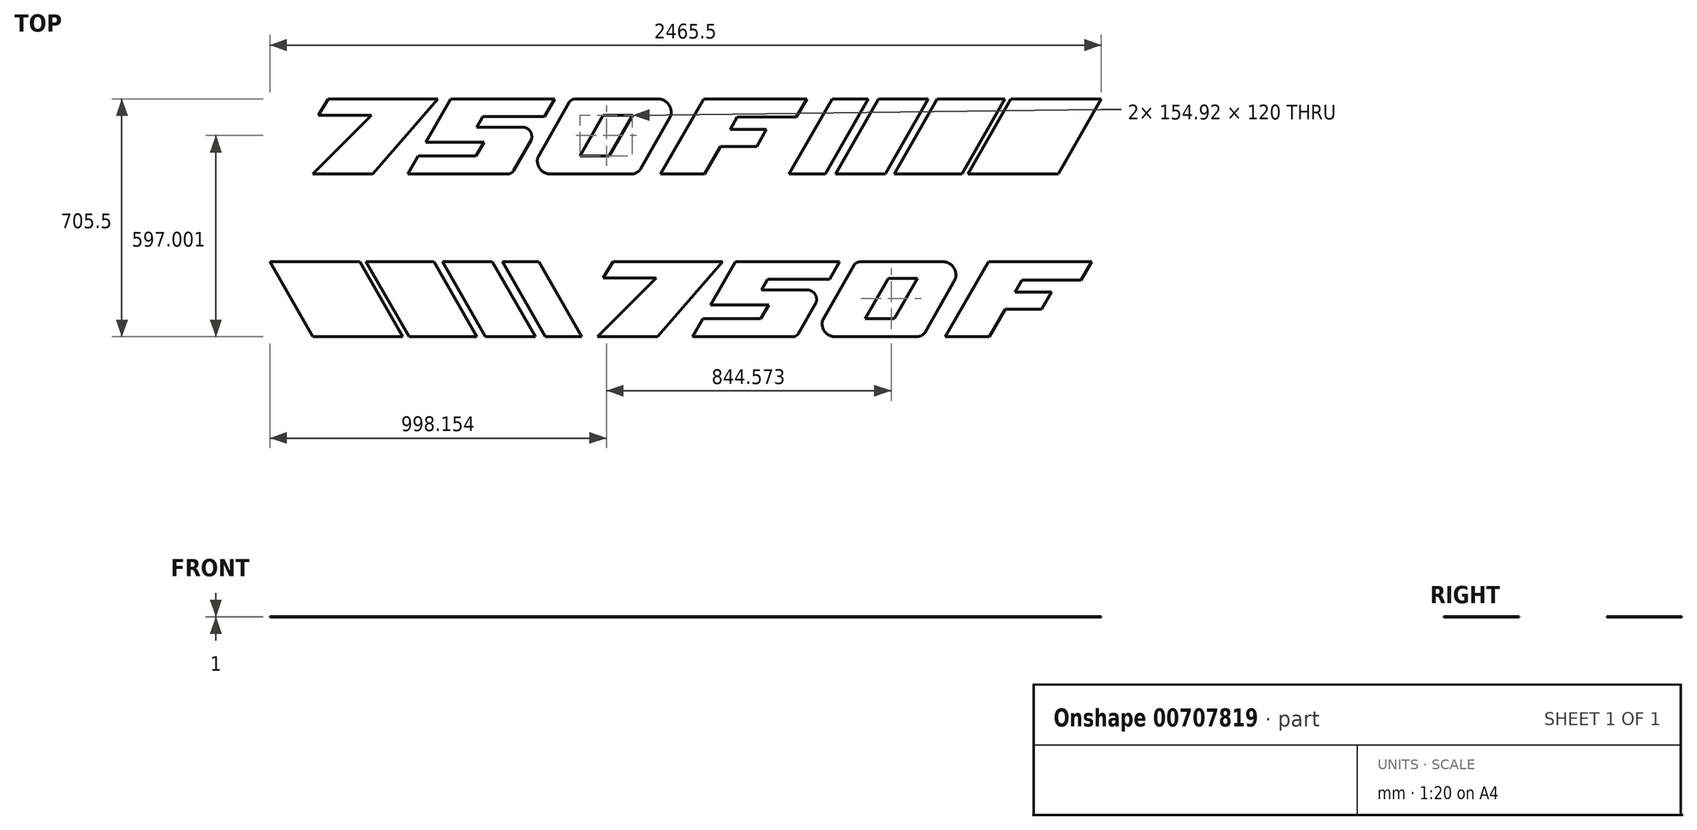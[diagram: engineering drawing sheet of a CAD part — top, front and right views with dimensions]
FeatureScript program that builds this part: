
annotation { "Feature Type Name" : "Feature", "Feature Type Description" : "" }
export const myFeature = defineFeature(function(context is Context, id is Id, definition is map)
    precondition{}
    {
        {
            var Q0;
            Q0=qCreatedBy(makeId("Top.planeOp"),FACE);
            var sketch = newSketch(context, id + "F0", { "sketchPlane" : qUnion([Q0])});
            skLineSegment(sketch, "E0", {"start": v(-1075.65, 281.14) * mm, "end": v(-750.23, 281.14) * mm});
            skLineSegment(sketch, "E1", {"start": v(-839.48, 58.67) * mm, "end": v(-542.36, 58.67) * mm});
            skLineSegment(sketch, "E2", {"start": v(-1105.04, 233.16) * mm, "end": v(-1075.65, 281.14) * mm});
            skLineSegment(sketch, "E3", {"start": v(-1105.04, 233.16) * mm, "end": v(-946.87, 233.16) * mm});
            skLineSegment(sketch, "E4", {"start": v(-946.87, 233.16) * mm, "end": v(-1121.46, 58.67) * mm});
            skLineSegment(sketch, "E5", {"start": v(-1121.46, 58.67) * mm, "end": v(-943.52, 58.67) * mm});
            skLineSegment(sketch, "E6", {"start": v(418.91, 281.14) * mm, "end": v(291.85, 58.67) * mm});
            skLineSegment(sketch, "E7", {"start": v(526.29, 281.14) * mm, "end": v(399.23, 58.67) * mm});
            skLineSegment(sketch, "E8", {"start": v(556.71, 281.14) * mm, "end": v(429.65, 58.67) * mm});
            skLineSegment(sketch, "E9", {"start": v(704.09, 281.14) * mm, "end": v(577.03, 58.67) * mm});
            skLineSegment(sketch, "E10", {"start": v(730.63, 281.14) * mm, "end": v(603.57, 58.67) * mm});
            skLineSegment(sketch, "E11", {"start": v(931.31, 281.14) * mm, "end": v(804.25, 58.67) * mm});
            skLineSegment(sketch, "E12", {"start": v(949.16, 281.14) * mm, "end": v(822.1, 58.67) * mm});
            skLineSegment(sketch, "E13", {"start": v(1216.97, 281.14) * mm, "end": v(1089.9, 58.67) * mm});
            skLineSegment(sketch, "E14", {"start": v(37.9, 281.14) * mm, "end": v(-89.16, 58.67) * mm});
            skLineSegment(sketch, "E15", {"start": v(137.83, 227.23) * mm, "end": v(117, 190.76) * mm});
            skLineSegment(sketch, "E16", {"start": v(344.12, 281.14) * mm, "end": v(313.33, 227.23) * mm});
            skLineSegment(sketch, "E17", {"start": v(137.83, 227.23) * mm, "end": v(313.33, 227.23) * mm});
            skLineSegment(sketch, "E18", {"start": v(117, 190.76) * mm, "end": v(224.56, 190.76) * mm});
            skLineSegment(sketch, "E19", {"start": v(88.26, 140.43) * mm, "end": v(195.82, 140.43) * mm});
            skLineSegment(sketch, "E20.trimOffspring", {"start": v(224.56, 190.76) * mm, "end": v(195.82, 140.43) * mm});
            skLineSegment(sketch, "E21.trimOffspring", {"start": v(88.26, 140.43) * mm, "end": v(41.56, 58.67) * mm});
            skLineSegment(sketch, "E22", {"start": v(-943.52, 58.67) * mm, "end": v(-750.23, 281.14) * mm});
            skLineSegment(sketch, "E23", {"start": v(-712.42, 281.14) * mm, "end": v(-785.6, 153.03) * mm});
            skLineSegment(sketch, "E24", {"start": v(-403.6, 281.14) * mm, "end": v(-433.3, 229.15) * mm});
            skLineSegment(sketch, "E25", {"start": v(-360.22, 271.8) * mm, "end": v(-453.2, 109) * mm});
            skLineSegment(sketch, "E26", {"start": v(-259.3, 232.64) * mm, "end": v(-327.84, 112.64) * mm});
            skLineSegment(sketch, "E27", {"start": v(-172.92, 232.64) * mm, "end": v(-241.45, 112.64) * mm});
            skLineSegment(sketch, "E28", {"start": v(-60.53, 229.18) * mm, "end": v(-150, 72.51) * mm});
            skLineSegment(sketch, "E29", {"start": v(-785.6, 153.03) * mm, "end": v(-613.24, 153.03) * mm});
            skLineSegment(sketch, "E30", {"start": v(-613.24, 153.03) * mm, "end": v(-636.6, 112.13) * mm});
            skLineSegment(sketch, "E31", {"start": v(-636.6, 112.13) * mm, "end": v(-808.95, 112.13) * mm});
            skLineSegment(sketch, "E32", {"start": v(-433.3, 229.15) * mm, "end": v(-616.43, 229.15) * mm});
            skLineSegment(sketch, "E33", {"start": v(-616.43, 229.15) * mm, "end": v(-634.47, 197.56) * mm});
            skLineSegment(sketch, "E34", {"start": v(-634.47, 197.56) * mm, "end": v(-496.87, 197.56) * mm});
            skLineSegment(sketch, "E35", {"start": v(-259.3, 232.64) * mm, "end": v(-172.92, 232.64) * mm});
            skLineSegment(sketch, "E36", {"start": v(-327.84, 112.64) * mm, "end": v(-241.45, 112.64) * mm});
            skLineSegment(sketch, "E37.trimOffspring", {"start": v(-808.95, 112.13) * mm, "end": v(-839.48, 58.67) * mm});
            skLineSegment(sketch, "E38.trimOffspring", {"start": v(-472.9, 159.8) * mm, "end": v(-524.88, 68.8) * mm});
            skLineSegment(sketch, "E39.trimOffspring", {"start": v(-712.42, 281.14) * mm, "end": v(-403.6, 281.14) * mm});
            skLineSegment(sketch, "E40.trimOffspring", {"start": v(-344.14, 281.14) * mm, "end": v(-92.2, 281.14) * mm});
            skLineSegment(sketch, "E41.trimOffspring", {"start": v(-416.83, 58.67) * mm, "end": v(-174.5, 58.67) * mm});
            skLineSegment(sketch, "E42.trimOffspring", {"start": v(-89.16, 58.67) * mm, "end": v(41.56, 58.67) * mm});
            skLineSegment(sketch, "E43.trimOffspring", {"start": v(37.9, 281.14) * mm, "end": v(344.12, 281.14) * mm});
            skLineSegment(sketch, "E44.trimOffspring", {"start": v(418.91, 281.14) * mm, "end": v(526.29, 281.14) * mm});
            skLineSegment(sketch, "E45.trimOffspring", {"start": v(291.85, 58.67) * mm, "end": v(399.23, 58.67) * mm});
            skLineSegment(sketch, "E46.trimOffspring", {"start": v(429.65, 58.67) * mm, "end": v(577.03, 58.67) * mm});
            skLineSegment(sketch, "E47.trimOffspring", {"start": v(556.71, 281.14) * mm, "end": v(704.09, 281.14) * mm});
            skLineSegment(sketch, "E48.trimOffspring", {"start": v(603.57, 58.67) * mm, "end": v(804.25, 58.67) * mm});
            skLineSegment(sketch, "E49.trimOffspring", {"start": v(730.63, 281.14) * mm, "end": v(931.31, 281.14) * mm});
            skLineSegment(sketch, "E50.trimOffspring", {"start": v(949.16, 281.14) * mm, "end": v(1216.97, 281.14) * mm});
            skLineSegment(sketch, "E51.trimOffspring", {"start": v(822.1, 58.67) * mm, "end": v(1089.9, 58.67) * mm});
            skArc(sketch, "E52", {"start": v(-472.9, 159.8) * mm, "mid": v(-475.61, 184.57) * mm, "end": v(-496.87, 197.56) * mm});
            skArc(sketch, "E53", {"start": v(-542.36, 58.67) * mm, "mid": v(-532.33, 61.52) * mm, "end": v(-524.88, 68.8) * mm});
            skArc(sketch, "E54", {"start": v(-453.2, 109) * mm, "mid": v(-447.59, 74.75) * mm, "end": v(-416.83, 58.67) * mm});
            skArc(sketch, "E55", {"start": v(-60.53, 229.18) * mm, "mid": v(-63.93, 262.74) * mm, "end": v(-92.2, 281.14) * mm});
            skArc(sketch, "E56", {"start": v(-174.5, 58.67) * mm, "mid": v(-160.63, 62.73) * mm, "end": v(-150, 72.51) * mm});
            skArc(sketch, "E57", {"start": v(-344.14, 281.14) * mm, "mid": v(-353.26, 278.33) * mm, "end": v(-360.22, 271.8) * mm});
            skLineSegment(sketch, "E58", {"start": v(-231.08, -201.9) * mm, "end": v(94.34, -201.9) * mm});
            skLineSegment(sketch, "E59", {"start": v(5.09, -424.36) * mm, "end": v(302.22, -424.36) * mm});
            skLineSegment(sketch, "E60", {"start": v(-260.47, -249.87) * mm, "end": v(-231.08, -201.9) * mm});
            skLineSegment(sketch, "E61", {"start": v(-260.47, -249.87) * mm, "end": v(-102.3, -249.87) * mm});
            skLineSegment(sketch, "E62", {"start": v(-102.3, -249.87) * mm, "end": v(-276.9, -424.36) * mm});
            skLineSegment(sketch, "E63", {"start": v(-276.9, -424.36) * mm, "end": v(-98.95, -424.36) * mm});
            skLineSegment(sketch, "E64", {"start": v(882.48, -201.9) * mm, "end": v(755.41, -424.36) * mm});
            skLineSegment(sketch, "E65", {"start": v(982.4, -255.8) * mm, "end": v(961.58, -292.27) * mm});
            skLineSegment(sketch, "E66", {"start": v(1188.7, -201.9) * mm, "end": v(1157.9, -255.8) * mm});
            skLineSegment(sketch, "E67", {"start": v(982.4, -255.8) * mm, "end": v(1157.9, -255.8) * mm});
            skLineSegment(sketch, "E68", {"start": v(961.58, -292.27) * mm, "end": v(1069.14, -292.27) * mm});
            skLineSegment(sketch, "E69", {"start": v(932.83, -342.6) * mm, "end": v(1040.4, -342.6) * mm});
            skLineSegment(sketch, "E70.trimOffspring", {"start": v(1069.14, -292.27) * mm, "end": v(1040.4, -342.6) * mm});
            skLineSegment(sketch, "E71.trimOffspring", {"start": v(932.83, -342.6) * mm, "end": v(886.14, -424.36) * mm});
            skLineSegment(sketch, "E72", {"start": v(-98.95, -424.36) * mm, "end": v(94.34, -201.9) * mm});
            skLineSegment(sketch, "E73", {"start": v(132.15, -201.9) * mm, "end": v(58.98, -330) * mm});
            skLineSegment(sketch, "E74", {"start": v(440.97, -201.9) * mm, "end": v(411.28, -253.88) * mm});
            skLineSegment(sketch, "E75", {"start": v(484.35, -211.23) * mm, "end": v(391.37, -374.03) * mm});
            skLineSegment(sketch, "E76", {"start": v(585.27, -250.4) * mm, "end": v(516.74, -370.4) * mm});
            skLineSegment(sketch, "E77", {"start": v(671.66, -250.4) * mm, "end": v(603.12, -370.4) * mm});
            skLineSegment(sketch, "E78", {"start": v(784.05, -253.85) * mm, "end": v(694.56, -410.52) * mm});
            skLineSegment(sketch, "E79", {"start": v(58.98, -330) * mm, "end": v(231.34, -330) * mm});
            skLineSegment(sketch, "E80", {"start": v(231.34, -330) * mm, "end": v(207.97, -370.9) * mm});
            skLineSegment(sketch, "E81", {"start": v(207.97, -370.9) * mm, "end": v(35.62, -370.9) * mm});
            skLineSegment(sketch, "E82", {"start": v(411.28, -253.88) * mm, "end": v(228.14, -253.88) * mm});
            skLineSegment(sketch, "E83", {"start": v(228.14, -253.88) * mm, "end": v(210.1, -285.47) * mm});
            skLineSegment(sketch, "E84", {"start": v(210.1, -285.47) * mm, "end": v(347.7, -285.47) * mm});
            skLineSegment(sketch, "E85", {"start": v(585.27, -250.4) * mm, "end": v(671.66, -250.4) * mm});
            skLineSegment(sketch, "E86", {"start": v(516.74, -370.4) * mm, "end": v(603.12, -370.4) * mm});
            skLineSegment(sketch, "E87.trimOffspring", {"start": v(35.62, -370.9) * mm, "end": v(5.09, -424.36) * mm});
            skLineSegment(sketch, "E88.trimOffspring", {"start": v(371.67, -323.24) * mm, "end": v(319.7, -414.23) * mm});
            skLineSegment(sketch, "E89.trimOffspring", {"start": v(132.15, -201.9) * mm, "end": v(440.97, -201.9) * mm});
            skLineSegment(sketch, "E90.trimOffspring", {"start": v(500.43, -201.9) * mm, "end": v(752.38, -201.9) * mm});
            skLineSegment(sketch, "E91.trimOffspring", {"start": v(427.74, -424.36) * mm, "end": v(670.07, -424.36) * mm});
            skLineSegment(sketch, "E92.trimOffspring", {"start": v(755.41, -424.36) * mm, "end": v(886.14, -424.36) * mm});
            skLineSegment(sketch, "E93.trimOffspring", {"start": v(882.48, -201.9) * mm, "end": v(1188.7, -201.9) * mm});
            skArc(sketch, "E94", {"start": v(371.67, -323.24) * mm, "mid": v(368.96, -298.47) * mm, "end": v(347.7, -285.47) * mm});
            skArc(sketch, "E95", {"start": v(302.22, -424.36) * mm, "mid": v(312.24, -421.5) * mm, "end": v(319.7, -414.23) * mm});
            skArc(sketch, "E96", {"start": v(391.37, -374.03) * mm, "mid": v(396.99, -408.28) * mm, "end": v(427.74, -424.36) * mm});
            skArc(sketch, "E97", {"start": v(784.05, -253.85) * mm, "mid": v(780.65, -220.3) * mm, "end": v(752.38, -201.9) * mm});
            skArc(sketch, "E98", {"start": v(670.07, -424.36) * mm, "mid": v(683.94, -420.3) * mm, "end": v(694.56, -410.52) * mm});
            skArc(sketch, "E99", {"start": v(500.43, -201.9) * mm, "mid": v(491.32, -204.7) * mm, "end": v(484.35, -211.23) * mm});
            skLineSegment(sketch, "E100.MirrorCS", {"start": v(-323.4, -424.36) * mm, "end": v(-430.78, -424.36) * mm});
            skLineSegment(sketch, "E101.MirrorCS", {"start": v(-588.27, -201.9) * mm, "end": v(-461.2, -424.36) * mm});
            skLineSegment(sketch, "E102.MirrorCS", {"start": v(-635.13, -424.36) * mm, "end": v(-835.81, -424.36) * mm});
            skLineSegment(sketch, "E103.MirrorCS", {"start": v(-853.66, -424.36) * mm, "end": v(-1121.46, -424.36) * mm});
            skLineSegment(sketch, "E104.MirrorCS", {"start": v(-762.2, -201.9) * mm, "end": v(-635.13, -424.36) * mm});
            skLineSegment(sketch, "E105.MirrorCS", {"start": v(-735.65, -201.9) * mm, "end": v(-608.58, -424.36) * mm});
            skLineSegment(sketch, "E106.MirrorCS", {"start": v(-762.2, -201.9) * mm, "end": v(-962.87, -201.9) * mm});
            skLineSegment(sketch, "E107.MirrorCS", {"start": v(-962.87, -201.9) * mm, "end": v(-835.81, -424.36) * mm});
            skLineSegment(sketch, "E108.MirrorCS", {"start": v(-980.72, -201.9) * mm, "end": v(-1248.53, -201.9) * mm});
            skLineSegment(sketch, "E109.MirrorCS", {"start": v(-450.47, -201.9) * mm, "end": v(-323.4, -424.36) * mm});
            skLineSegment(sketch, "E110.MirrorCS", {"start": v(-557.85, -201.9) * mm, "end": v(-430.78, -424.36) * mm});
            skLineSegment(sketch, "E111.MirrorCS", {"start": v(-980.72, -201.9) * mm, "end": v(-853.66, -424.36) * mm});
            skLineSegment(sketch, "E112.MirrorCS", {"start": v(-461.2, -424.36) * mm, "end": v(-608.58, -424.36) * mm});
            skLineSegment(sketch, "E113.MirrorCS", {"start": v(-1248.53, -201.9) * mm, "end": v(-1121.46, -424.36) * mm});
            skLineSegment(sketch, "E114.MirrorCS", {"start": v(-450.47, -201.9) * mm, "end": v(-557.85, -201.9) * mm});
            skLineSegment(sketch, "E115.MirrorCS", {"start": v(-588.27, -201.9) * mm, "end": v(-735.65, -201.9) * mm});
            skSolve(sketch);
        }
        {
            var Q0;
            Q0=makeQuery(id+"F0.imprint","IMPRINT",FACE,{"disambiguationData":[TD([[makeQuery(id+"F0.imprint","IMPRINT",EDGE,{"derivedFrom":sQuery(id+"F0.wireOp",EDGE,"E75")}),1.0]])]});
            var Q1;
            Q1=makeQuery(id+"F0.imprint","IMPRINT",FACE,{"disambiguationData":[TD([[makeQuery(id+"F0.imprint","IMPRINT",EDGE,{"derivedFrom":sQuery(id+"F0.wireOp",EDGE,"E103.MirrorCS")}),-1.0]])]});
            var Q2;
            Q2=makeQuery(id+"F0.imprint","IMPRINT",FACE,{"disambiguationData":[TD([[makeQuery(id+"F0.imprint","IMPRINT",EDGE,{"derivedFrom":sQuery(id+"F0.wireOp",EDGE,"E25")}),1.0]])]});
            var Q3;
            Q3=makeQuery(id+"F0.imprint","IMPRINT",FACE,{"disambiguationData":[TD([[makeQuery(id+"F0.imprint","IMPRINT",EDGE,{"derivedFrom":sQuery(id+"F0.wireOp",EDGE,"E0")}),-1.0]])]});
            var Q4;
            Q4=makeQuery(id+"F0.imprint","IMPRINT",FACE,{"disambiguationData":[TD([[makeQuery(id+"F0.imprint","IMPRINT",EDGE,{"derivedFrom":sQuery(id+"F0.wireOp",EDGE,"E1")}),1.0]])]});
            var Q5;
            Q5=makeQuery(id+"F0.imprint","IMPRINT",FACE,{"disambiguationData":[TD([[makeQuery(id+"F0.imprint","IMPRINT",EDGE,{"derivedFrom":sQuery(id+"F0.wireOp",EDGE,"E6")}),1.0]])]});
            var Q6;
            Q6=makeQuery(id+"F0.imprint","IMPRINT",FACE,{"disambiguationData":[TD([[makeQuery(id+"F0.imprint","IMPRINT",EDGE,{"derivedFrom":sQuery(id+"F0.wireOp",EDGE,"E8")}),1.0]])]});
            var Q7;
            Q7=makeQuery(id+"F0.imprint","IMPRINT",FACE,{"disambiguationData":[TD([[makeQuery(id+"F0.imprint","IMPRINT",EDGE,{"derivedFrom":sQuery(id+"F0.wireOp",EDGE,"E10")}),1.0]])]});
            var Q8;
            Q8=makeQuery(id+"F0.imprint","IMPRINT",FACE,{"disambiguationData":[TD([[makeQuery(id+"F0.imprint","IMPRINT",EDGE,{"derivedFrom":sQuery(id+"F0.wireOp",EDGE,"E12")}),1.0]])]});
            var Q9;
            Q9=makeQuery(id+"F0.imprint","IMPRINT",FACE,{"disambiguationData":[TD([[makeQuery(id+"F0.imprint","IMPRINT",EDGE,{"derivedFrom":sQuery(id+"F0.wireOp",EDGE,"E14")}),1.0]])]});
            var Q10;
            Q10=makeQuery(id+"F0.imprint","IMPRINT",FACE,{"disambiguationData":[TD([[makeQuery(id+"F0.imprint","IMPRINT",EDGE,{"derivedFrom":sQuery(id+"F0.wireOp",EDGE,"E58")}),-1.0]])]});
            var Q11;
            Q11=makeQuery(id+"F0.imprint","IMPRINT",FACE,{"disambiguationData":[TD([[makeQuery(id+"F0.imprint","IMPRINT",EDGE,{"derivedFrom":sQuery(id+"F0.wireOp",EDGE,"E59")}),1.0]])]});
            var Q12;
            Q12=makeQuery(id+"F0.imprint","IMPRINT",FACE,{"disambiguationData":[TD([[makeQuery(id+"F0.imprint","IMPRINT",EDGE,{"derivedFrom":sQuery(id+"F0.wireOp",EDGE,"E64")}),1.0]])]});
            var Q13;
            Q13=makeQuery(id+"F0.imprint","IMPRINT",FACE,{"disambiguationData":[TD([[makeQuery(id+"F0.imprint","IMPRINT",EDGE,{"derivedFrom":sQuery(id+"F0.wireOp",EDGE,"E100.MirrorCS")}),-1.0]])]});
            var Q14;
            Q14=makeQuery(id+"F0.imprint","IMPRINT",FACE,{"disambiguationData":[TD([[makeQuery(id+"F0.imprint","IMPRINT",EDGE,{"derivedFrom":sQuery(id+"F0.wireOp",EDGE,"E101.MirrorCS")}),-1.0]])]});
            var Q15;
            Q15=makeQuery(id+"F0.imprint","IMPRINT",FACE,{"disambiguationData":[TD([[makeQuery(id+"F0.imprint","IMPRINT",EDGE,{"derivedFrom":sQuery(id+"F0.wireOp",EDGE,"E102.MirrorCS")}),-1.0]])]});
            extrude(context, id + "F1", {"entities" : qUnion([Q0, Q1, Q2, Q3, Q4, Q5, Q6, Q7, Q8, Q9, Q10, Q11, Q12, Q13, Q14, Q15]), "depth" : 1 * mm, "offsetDistance" : 25 * mm});
        }
    });
